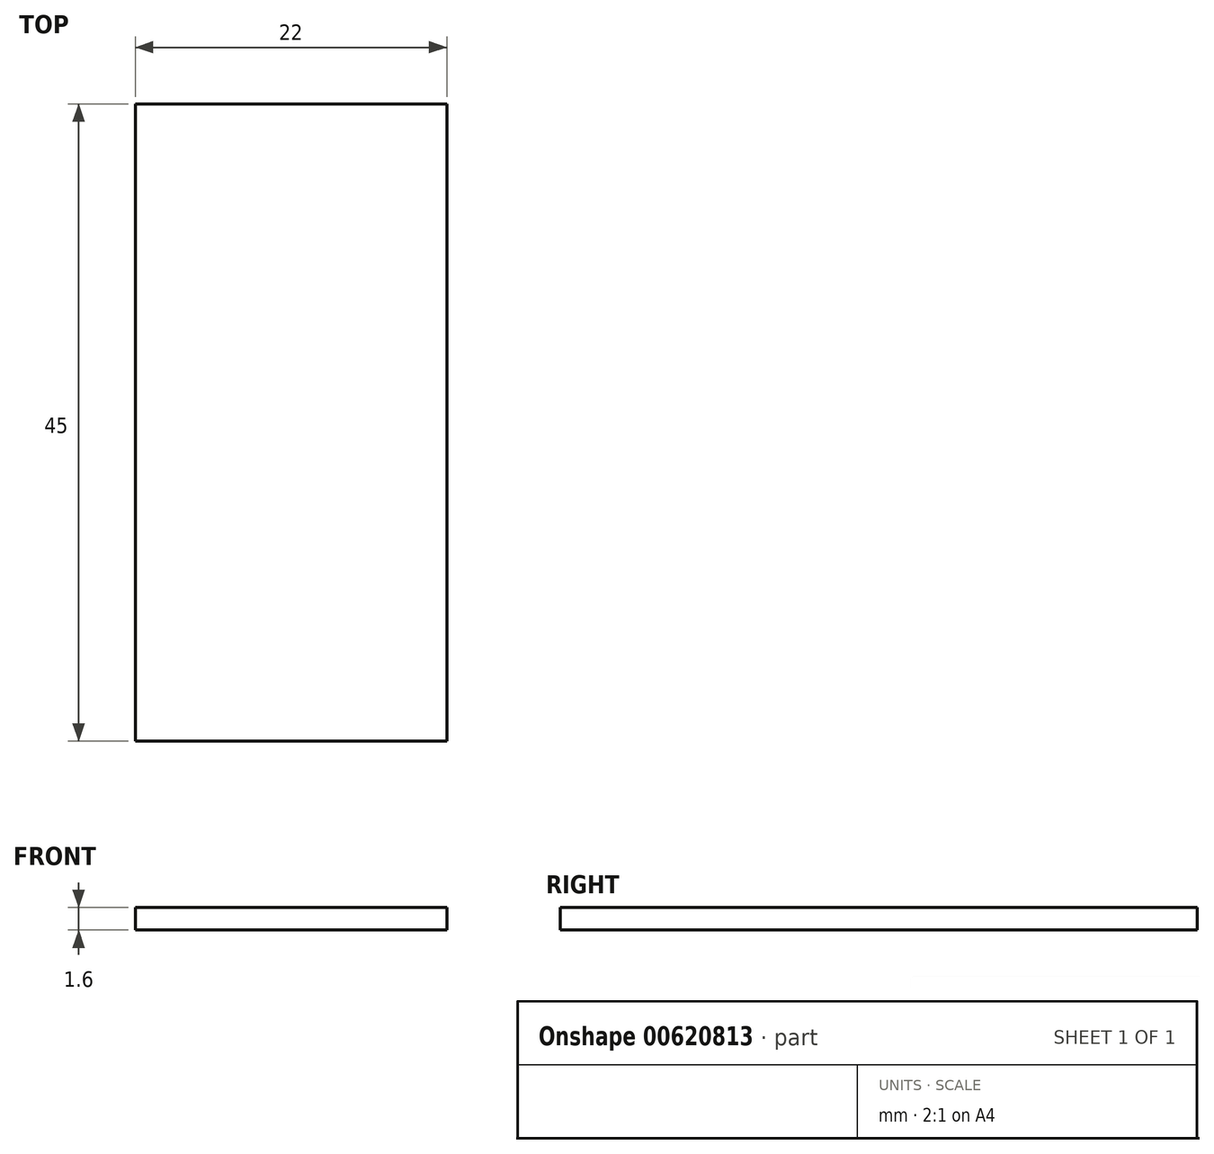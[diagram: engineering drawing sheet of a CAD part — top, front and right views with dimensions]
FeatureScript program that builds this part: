
annotation { "Feature Type Name" : "Feature", "Feature Type Description" : "" }
export const myFeature = defineFeature(function(context is Context, id is Id, definition is map)
    precondition{}
    {
        {
            var Q0;
            Q0=qCreatedBy(makeId("Top.planeOp"),FACE);
            var sketch = newSketch(context, id + "F0", { "sketchPlane" : qUnion([Q0])});
            skLineSegment(sketch, "E0.bottom", {"start": v(0, 0) * mm, "end": v(22, 0) * mm});
            skLineSegment(sketch, "E0.top", {"start": v(0, 45) * mm, "end": v(22, 45) * mm});
            skLineSegment(sketch, "E0.left", {"start": v(0, 0) * mm, "end": v(0, 45) * mm});
            skLineSegment(sketch, "E0.right", {"start": v(22, 0) * mm, "end": v(22, 45) * mm});
            skSolve(sketch);
        }
        {
            var Q0;
            Q0 = qSketchRegion(id + "F0", true);
            extrude(context, id + "F1", {"entities" : qUnion([Q0]), "depth" : 1.6 * mm, "offsetDistance" : 25 * mm});
        }
    });
